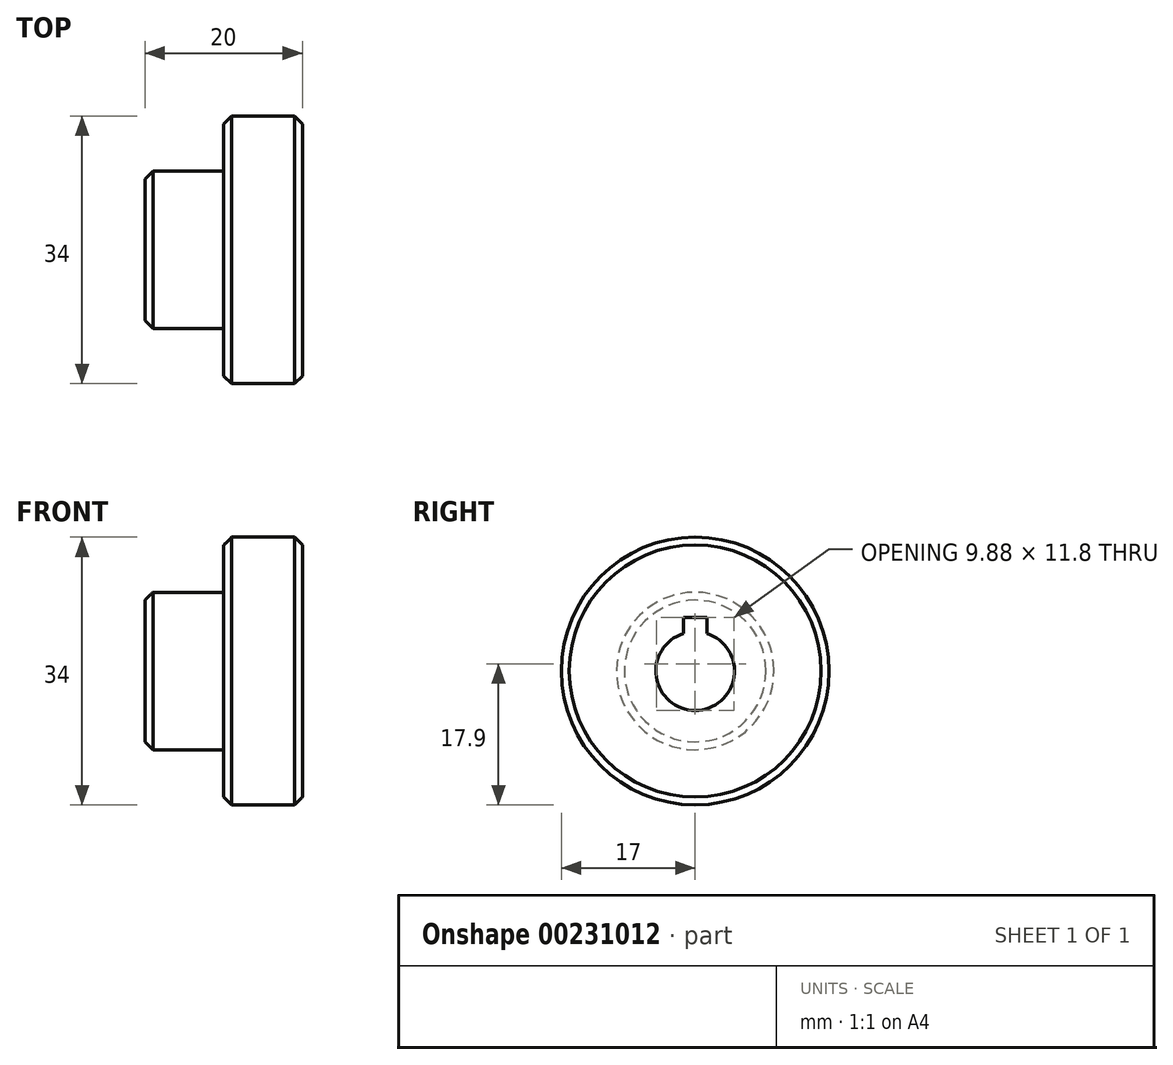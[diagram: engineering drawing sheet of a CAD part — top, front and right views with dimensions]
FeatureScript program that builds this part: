
annotation { "Feature Type Name" : "Feature", "Feature Type Description" : "" }
export const myFeature = defineFeature(function(context is Context, id is Id, definition is map)
    precondition{}
    {
        {
            var Q0;
            Q0=qCreatedBy(makeId("Top.planeOp"),FACE);
            var sketch = newSketch(context, id + "F0", { "sketchPlane" : qUnion([Q0])});
            skLineSegment(sketch, "E0", {"start": v(0, 0) * mm, "end": v(0, 10) * mm});
            skLineSegment(sketch, "E1", {"start": v(0, 10) * mm, "end": v(10, 10) * mm});
            skLineSegment(sketch, "E2", {"start": v(10, 10) * mm, "end": v(10, 17) * mm});
            skLineSegment(sketch, "E3", {"start": v(10, 17) * mm, "end": v(20, 17) * mm});
            skLineSegment(sketch, "E4", {"start": v(20, 17) * mm, "end": v(20, 5) * mm});
            skLineSegment(sketch, "E5", {"start": v(20, 5) * mm, "end": v(0, 5) * mm});
            skLineSegment(sketch, "E6", {"start": v(-11.06, 0) * mm, "end": v(87.21, 0) * mm, "construction": true});
            skSolve(sketch);
        }
        {
            var Q0;
            {var subQ0=sQuery(id+"F0.wireOp",EDGE,"E1");Q0=makeQuery(id+"F0.imprint","IMPRINT",FACE,{"disambiguationData":[TD([[makeQuery(id+"F0.imprint","IMPRINT",EDGE,{"derivedFrom":subQ0}),-1.0]])]});}
            var Q1;
            Q1=sQuery(id+"F0.wireOp",EDGE,"E6");
            revolve(context, id + "F1", {"entities" : qUnion([Q0]), "axis" : qUnion([Q1]), "revolveType" : RevolveType.FULL});
        }
        {
            var Q0;
            Q0=makeQuery(id+"F1.opRevolve","SWEPT_EDGE",EDGE,{"disambiguationData":[OSD([sQuery(id+"F0.wireOp",EDGE,"E0"),sQuery(id+"F0.wireOp",EDGE,"E1")])]});
            var Q1;
            Q1=makeQuery(id+"F1.opRevolve","SWEPT_EDGE",EDGE,{"disambiguationData":[OSD([sQuery(id+"F0.wireOp",EDGE,"E2"),sQuery(id+"F0.wireOp",EDGE,"E3")])]});
            var Q2;
            Q2=makeQuery(id+"F1.opRevolve","SWEPT_EDGE",EDGE,{"disambiguationData":[OSD([sQuery(id+"F0.wireOp",EDGE,"E3"),sQuery(id+"F0.wireOp",EDGE,"E4")])]});
            chamfer(context, id + "F2", {"entities" : qUnion([Q0, Q1, Q2]), "width" : 1 * mm, "tangentPropagation" : true});
        }
        {
            var Q0;
            Q0=makeQuery(id+"F1.opRevolve","SWEPT_FACE",FACE,{"disambiguationData":[OSD([sQuery(id+"F0.wireOp",EDGE,"E0")])]});
            var sketch = newSketch(context, id + "F3", { "sketchPlane" : qUnion([Q0])});
            skLineSegment(sketch, "E7", {"start": v(0, 6.8) * mm, "end": v(1.5, 6.8) * mm});
            skLineSegment(sketch, "E8", {"start": v(1.5, 6.8) * mm, "end": v(1.5, 4.77) * mm});
            skLineSegment(sketch, "E9", {"start": v(0, 6.8) * mm, "end": v(-1.5, 6.8) * mm});
            skLineSegment(sketch, "E10", {"start": v(-1.5, 6.8) * mm, "end": v(-1.5, 4.77) * mm});
            skPoint(sketch, "E11.start.orphan", {"position": v(0, -5) * mm});
            skSolve(sketch);
        }
        {
            var Q0;
            Q0=makeQuery(id+"F3.imprint","IMPRINT",FACE,{"disambiguationData":[TD([[makeQuery(id+"F3.imprint","IMPRINT",EDGE,{"derivedFrom":sQuery(id+"F3.wireOp",EDGE,"E7")}),-1.0]])]});
            extrude(context, id + "F4", {"entities" : qUnion([Q0]), "operationType" : NewBodyOperationType.REMOVE, "oppositeDirection" : true, "depth" : 20 * mm});
        }
    });
